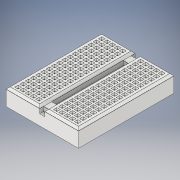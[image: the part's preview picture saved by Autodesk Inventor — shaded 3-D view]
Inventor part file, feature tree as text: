
AUTODESK INVENTOR PART (.ipt)
format: ipt  version: 2019 (Build 230136000, 136)  size: 1,296,384 bytes
history: mixed  units: in
note: dims shown in document units (in); Inventor stores cm internally (conversion verified against a paired STEP export)
features: fillet x1, imported_body x1
ambient origin geometry x8: Origin, YZ Plane, XZ Plane, XY Plane, X Axis, Y Axis, Z Axis, Center Point
bodies: Solid1 (imported_parasolid)
feature tree (2):
  fillet  "Fillet4"  [1 undecoded]
  imported_body  NMx_Import_Brep_tag  [imported B-rep: ~2268 faces, bbox_mm=[34.6, 8.15, 45.6]]
note: 1 required parameter value undecoded (feature->parameter linkage not recoverable at this tier; creation-order binding heuristic only, values carry confidence <= 0.55)
